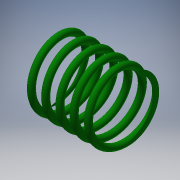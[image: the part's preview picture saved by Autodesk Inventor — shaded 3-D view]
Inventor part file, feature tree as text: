
AUTODESK INVENTOR PART (.ipt)
format: ipt  version: 2018 (Build 220112000, 112)  size: 357,376 bytes
history: native  units: mm
features: sketch x2, helix x1, extrude x1
ambient origin geometry x8: Origin, YZ Plane, XZ Plane, XY Plane, X Axis, Y Axis, Z Axis, Center Point
bodies: Solid1 (feature_tree)
feature tree (4):
  helix  "Coil1"  [1 undecoded]
  extrude  "Extrusion1"  Depth=11.4mm
  sketch  "Sketch1"  dims[d1=3.8mm]
  sketch  "Sketch2"  dims[d2=1.78mm d3=10.0mm d4=90.0mm d5=0.0mm d6=90.0deg d7=90.0deg d8=0.0mm d9=0.0mm d10=11.4mm d11=7.0mm d12=11.0mm d13=39.5mm d14=0.0mm]
note: 1 required parameter value undecoded (feature->parameter linkage not recoverable at this tier; creation-order binding heuristic only, values carry confidence <= 0.55)
